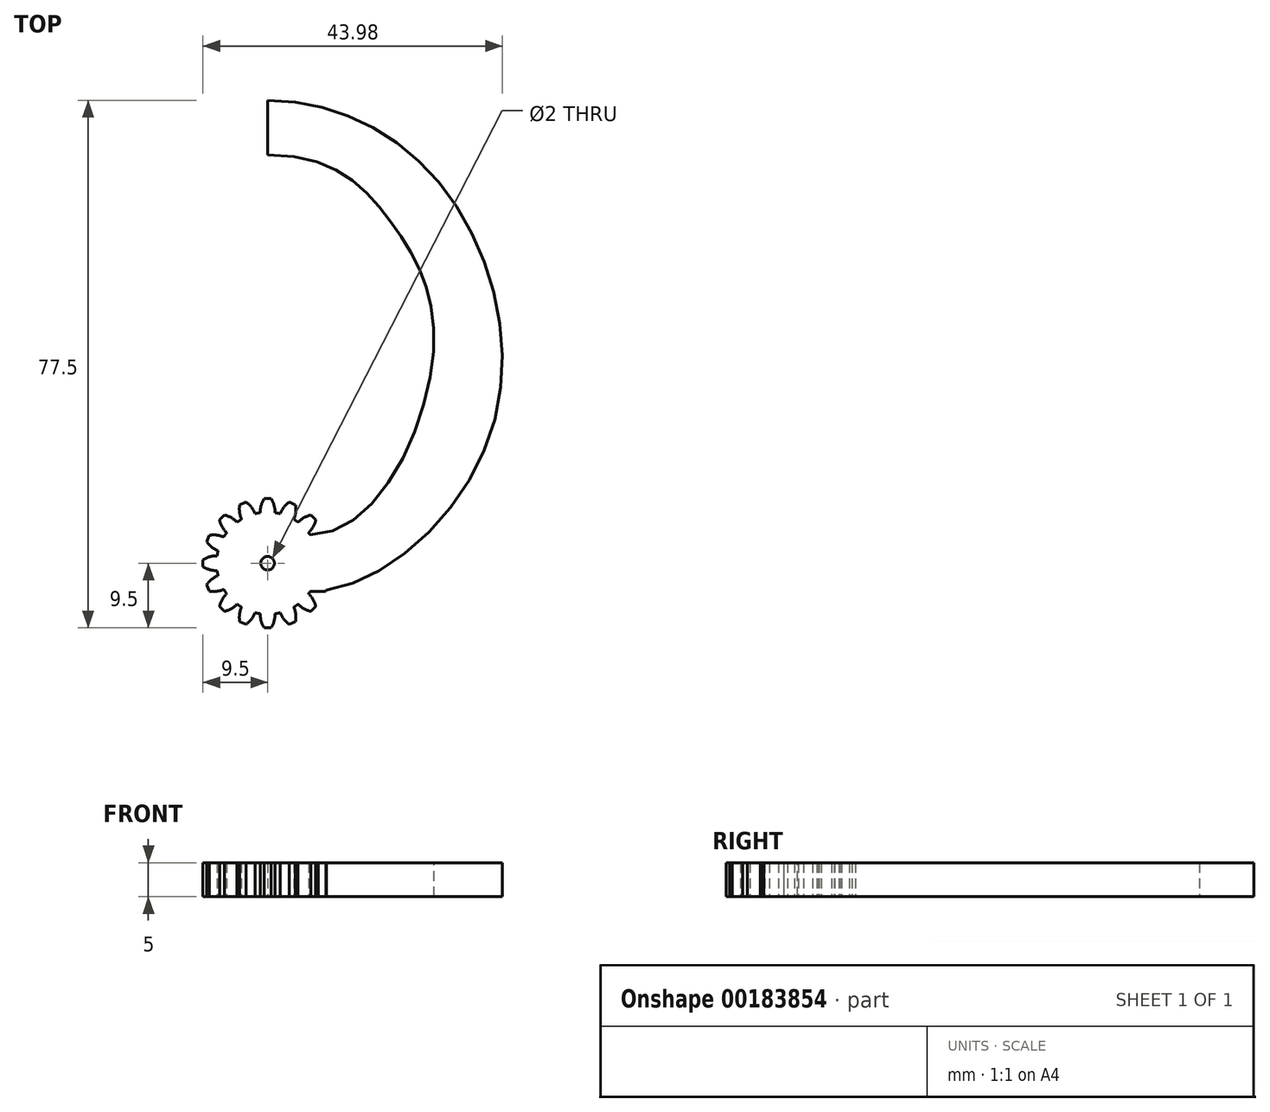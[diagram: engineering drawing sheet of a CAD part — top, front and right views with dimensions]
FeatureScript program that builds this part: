
annotation { "Feature Type Name" : "Feature", "Feature Type Description" : "" }
export const myFeature = defineFeature(function(context is Context, id is Id, definition is map)
    precondition{}
    {
        {
            var Q0;
            Q0=qCreatedBy(makeId("Top.planeOp"),FACE);
            var sketch = newSketch(context, id + "F0", { "sketchPlane" : qUnion([Q0])});
            skCircle(sketch, "E0", {"center": v(0, 0) * mm, "radius": 7.5 * mm});
            skLineSegment(sketch, "E1", {"start": v(0, 0) * mm, "end": v(0, 7.5) * mm, "construction": true});
            skLineSegment(sketch, "E2", {"start": v(0, 9.5) * mm, "end": v(-0.5, 9.5) * mm});
            skArc(sketch, "E3", {"start": v(-0.5, 9.5) * mm, "mid": v(-0.95, 8.5) * mm, "end": v(-1.09, 7.42) * mm});
            skLineSegment(sketch, "E4.MirrorCS", {"start": v(0, 9.5) * mm, "end": v(0.5, 9.5) * mm});
            skArc(sketch, "E5.MirrorCS", {"start": v(0.5, 9.5) * mm, "mid": v(0.95, 8.5) * mm, "end": v(1.09, 7.42) * mm});
            skArc(sketch, "E6.1.0", {"start": v(-4.1, 8.59) * mm, "mid": v(-4.13, 7.5) * mm, "end": v(-3.85, 6.44) * mm});
            skLineSegment(sketch, "E6.1.1", {"start": v(-3.64, 8.78) * mm, "end": v(-4.1, 8.59) * mm});
            skLineSegment(sketch, "E6.1.2", {"start": v(-3.64, 8.78) * mm, "end": v(-3.17, 8.97) * mm});
            skArc(sketch, "E6.1.3", {"start": v(-3.17, 8.97) * mm, "mid": v(-2.38, 8.22) * mm, "end": v(-1.83, 7.27) * mm});
            skArc(sketch, "E6.2.0", {"start": v(-7.07, 6.36) * mm, "mid": v(-6.69, 5.34) * mm, "end": v(-6.02, 4.48) * mm});
            skLineSegment(sketch, "E6.2.1", {"start": v(-6.72, 6.72) * mm, "end": v(-7.07, 6.36) * mm});
            skLineSegment(sketch, "E6.2.2", {"start": v(-6.72, 6.72) * mm, "end": v(-6.36, 7.07) * mm});
            skArc(sketch, "E6.2.3", {"start": v(-6.36, 7.07) * mm, "mid": v(-5.34, 6.69) * mm, "end": v(-4.48, 6.02) * mm});
            skArc(sketch, "E6.3.0", {"start": v(-8.97, 3.17) * mm, "mid": v(-8.22, 2.38) * mm, "end": v(-7.27, 1.83) * mm});
            skLineSegment(sketch, "E6.3.1", {"start": v(-8.78, 3.64) * mm, "end": v(-8.97, 3.17) * mm});
            skLineSegment(sketch, "E6.3.2", {"start": v(-8.78, 3.64) * mm, "end": v(-8.59, 4.1) * mm});
            skArc(sketch, "E6.3.3", {"start": v(-8.59, 4.1) * mm, "mid": v(-7.5, 4.13) * mm, "end": v(-6.44, 3.85) * mm});
            skArc(sketch, "E6.4.0", {"start": v(-9.5, -0.5) * mm, "mid": v(-8.5, -0.95) * mm, "end": v(-7.42, -1.09) * mm});
            skLineSegment(sketch, "E6.4.1", {"start": v(-9.5, 0) * mm, "end": v(-9.5, -0.5) * mm});
            skLineSegment(sketch, "E6.4.2", {"start": v(-9.5, 0) * mm, "end": v(-9.5, 0.5) * mm});
            skArc(sketch, "E6.4.3", {"start": v(-9.5, 0.5) * mm, "mid": v(-8.5, 0.95) * mm, "end": v(-7.42, 1.09) * mm});
            skArc(sketch, "E6.5.0", {"start": v(-8.59, -4.1) * mm, "mid": v(-7.5, -4.13) * mm, "end": v(-6.44, -3.85) * mm});
            skLineSegment(sketch, "E6.5.1", {"start": v(-8.78, -3.64) * mm, "end": v(-8.59, -4.1) * mm});
            skLineSegment(sketch, "E6.5.2", {"start": v(-8.78, -3.64) * mm, "end": v(-8.97, -3.17) * mm});
            skArc(sketch, "E6.5.3", {"start": v(-8.97, -3.17) * mm, "mid": v(-8.22, -2.38) * mm, "end": v(-7.27, -1.83) * mm});
            skArc(sketch, "E6.6.0", {"start": v(-6.36, -7.07) * mm, "mid": v(-5.34, -6.69) * mm, "end": v(-4.48, -6.02) * mm});
            skLineSegment(sketch, "E6.6.1", {"start": v(-6.72, -6.72) * mm, "end": v(-6.36, -7.07) * mm});
            skLineSegment(sketch, "E6.6.2", {"start": v(-6.72, -6.72) * mm, "end": v(-7.07, -6.36) * mm});
            skArc(sketch, "E6.6.3", {"start": v(-7.07, -6.36) * mm, "mid": v(-6.69, -5.34) * mm, "end": v(-6.02, -4.48) * mm});
            skArc(sketch, "E6.7.0", {"start": v(-3.17, -8.97) * mm, "mid": v(-2.38, -8.22) * mm, "end": v(-1.83, -7.27) * mm});
            skLineSegment(sketch, "E6.7.1", {"start": v(-3.64, -8.78) * mm, "end": v(-3.17, -8.97) * mm});
            skLineSegment(sketch, "E6.7.2", {"start": v(-3.64, -8.78) * mm, "end": v(-4.1, -8.59) * mm});
            skArc(sketch, "E6.7.3", {"start": v(-4.1, -8.59) * mm, "mid": v(-4.13, -7.5) * mm, "end": v(-3.85, -6.44) * mm});
            skArc(sketch, "E6.8.0", {"start": v(0.5, -9.5) * mm, "mid": v(0.95, -8.5) * mm, "end": v(1.09, -7.42) * mm});
            skLineSegment(sketch, "E6.8.1", {"start": v(0, -9.5) * mm, "end": v(0.5, -9.5) * mm});
            skLineSegment(sketch, "E6.8.2", {"start": v(0, -9.5) * mm, "end": v(-0.5, -9.5) * mm});
            skArc(sketch, "E6.8.3", {"start": v(-0.5, -9.5) * mm, "mid": v(-0.95, -8.5) * mm, "end": v(-1.09, -7.42) * mm});
            skArc(sketch, "E6.9.0", {"start": v(4.1, -8.59) * mm, "mid": v(4.13, -7.5) * mm, "end": v(3.85, -6.44) * mm});
            skLineSegment(sketch, "E6.9.1", {"start": v(3.64, -8.78) * mm, "end": v(4.1, -8.59) * mm});
            skLineSegment(sketch, "E6.9.2", {"start": v(3.64, -8.78) * mm, "end": v(3.17, -8.97) * mm});
            skArc(sketch, "E6.9.3", {"start": v(3.17, -8.97) * mm, "mid": v(2.38, -8.22) * mm, "end": v(1.83, -7.27) * mm});
            skArc(sketch, "E6.10.0", {"start": v(7.07, -6.36) * mm, "mid": v(6.69, -5.34) * mm, "end": v(6.02, -4.48) * mm});
            skLineSegment(sketch, "E6.10.1", {"start": v(6.72, -6.72) * mm, "end": v(7.07, -6.36) * mm});
            skLineSegment(sketch, "E6.10.2", {"start": v(6.72, -6.72) * mm, "end": v(6.36, -7.07) * mm});
            skArc(sketch, "E6.10.3", {"start": v(6.36, -7.07) * mm, "mid": v(5.34, -6.69) * mm, "end": v(4.48, -6.02) * mm});
            skArc(sketch, "E6.11.0", {"start": v(8.97, -3.17) * mm, "mid": v(8.22, -2.38) * mm, "end": v(7.27, -1.83) * mm});
            skLineSegment(sketch, "E6.11.1", {"start": v(8.78, -3.64) * mm, "end": v(8.97, -3.17) * mm});
            skLineSegment(sketch, "E6.11.2", {"start": v(8.78, -3.64) * mm, "end": v(8.59, -4.1) * mm});
            skArc(sketch, "E6.11.3", {"start": v(8.59, -4.1) * mm, "mid": v(7.5, -4.13) * mm, "end": v(6.44, -3.85) * mm});
            skArc(sketch, "E6.12.0", {"start": v(9.5, 0.5) * mm, "mid": v(8.5, 0.95) * mm, "end": v(7.42, 1.09) * mm});
            skLineSegment(sketch, "E6.12.1", {"start": v(9.5, 0) * mm, "end": v(9.5, 0.5) * mm});
            skLineSegment(sketch, "E6.12.2", {"start": v(9.5, 0) * mm, "end": v(9.5, -0.5) * mm});
            skArc(sketch, "E6.12.3", {"start": v(9.5, -0.5) * mm, "mid": v(8.5, -0.95) * mm, "end": v(7.42, -1.09) * mm});
            skArc(sketch, "E6.13.0", {"start": v(8.59, 4.1) * mm, "mid": v(7.5, 4.13) * mm, "end": v(6.44, 3.85) * mm});
            skLineSegment(sketch, "E6.13.1", {"start": v(8.78, 3.64) * mm, "end": v(8.59, 4.1) * mm});
            skLineSegment(sketch, "E6.13.2", {"start": v(8.78, 3.64) * mm, "end": v(8.97, 3.17) * mm});
            skArc(sketch, "E6.13.3", {"start": v(8.97, 3.17) * mm, "mid": v(8.22, 2.38) * mm, "end": v(7.27, 1.83) * mm});
            skArc(sketch, "E6.14.0", {"start": v(6.36, 7.07) * mm, "mid": v(5.34, 6.69) * mm, "end": v(4.48, 6.02) * mm});
            skLineSegment(sketch, "E6.14.1", {"start": v(6.72, 6.72) * mm, "end": v(6.36, 7.07) * mm});
            skLineSegment(sketch, "E6.14.2", {"start": v(6.72, 6.72) * mm, "end": v(7.07, 6.36) * mm});
            skArc(sketch, "E6.14.3", {"start": v(7.07, 6.36) * mm, "mid": v(6.69, 5.34) * mm, "end": v(6.02, 4.48) * mm});
            skArc(sketch, "E6.15.0", {"start": v(3.17, 8.97) * mm, "mid": v(2.38, 8.22) * mm, "end": v(1.83, 7.27) * mm});
            skLineSegment(sketch, "E6.15.1", {"start": v(3.64, 8.78) * mm, "end": v(3.17, 8.97) * mm});
            skLineSegment(sketch, "E6.15.2", {"start": v(3.64, 8.78) * mm, "end": v(4.1, 8.59) * mm});
            skArc(sketch, "E6.15.3", {"start": v(4.1, 8.59) * mm, "mid": v(4.13, 7.5) * mm, "end": v(3.85, 6.44) * mm});
            skSolve(sketch);
        }
        {
            var Q0;
            Q0=qSketchRegion(id+"F0",true);
            extrude(context, id + "F1", {"entities" : qUnion([Q0]), "depth" : 5 * mm});
        }
        {
            var Q0;
            Q0=makeQuery(id+"F1.opExtrude","CAP_FACE",FACE,{"disambiguationData":[OSD([sQuery(id+"F0.wireOp",EDGE,"E0"),sQuery(id+"F0.wireOp",EDGE,"E2"),sQuery(id+"F0.wireOp",EDGE,"E3"),sQuery(id+"F0.wireOp",EDGE,"E4.MirrorCS"),sQuery(id+"F0.wireOp",EDGE,"E5.MirrorCS"),sQuery(id+"F0.wireOp",EDGE,"E6.1.0"),sQuery(id+"F0.wireOp",EDGE,"E6.1.1"),sQuery(id+"F0.wireOp",EDGE,"E6.1.2"),sQuery(id+"F0.wireOp",EDGE,"E6.1.3"),sQuery(id+"F0.wireOp",EDGE,"E6.2.0"),sQuery(id+"F0.wireOp",EDGE,"E6.2.1"),sQuery(id+"F0.wireOp",EDGE,"E6.2.2"),sQuery(id+"F0.wireOp",EDGE,"E6.2.3"),sQuery(id+"F0.wireOp",EDGE,"E6.3.0"),sQuery(id+"F0.wireOp",EDGE,"E6.3.1"),sQuery(id+"F0.wireOp",EDGE,"E6.3.2"),sQuery(id+"F0.wireOp",EDGE,"E6.3.3"),sQuery(id+"F0.wireOp",EDGE,"E6.4.0"),sQuery(id+"F0.wireOp",EDGE,"E6.4.1"),sQuery(id+"F0.wireOp",EDGE,"E6.4.2"),sQuery(id+"F0.wireOp",EDGE,"E6.4.3"),sQuery(id+"F0.wireOp",EDGE,"E6.5.0"),sQuery(id+"F0.wireOp",EDGE,"E6.5.1"),sQuery(id+"F0.wireOp",EDGE,"E6.5.2"),sQuery(id+"F0.wireOp",EDGE,"E6.5.3"),sQuery(id+"F0.wireOp",EDGE,"E6.6.0"),sQuery(id+"F0.wireOp",EDGE,"E6.6.1"),sQuery(id+"F0.wireOp",EDGE,"E6.6.2"),sQuery(id+"F0.wireOp",EDGE,"E6.6.3"),sQuery(id+"F0.wireOp",EDGE,"E6.7.0"),sQuery(id+"F0.wireOp",EDGE,"E6.7.1"),sQuery(id+"F0.wireOp",EDGE,"E6.7.2"),sQuery(id+"F0.wireOp",EDGE,"E6.7.3"),sQuery(id+"F0.wireOp",EDGE,"E6.8.0"),sQuery(id+"F0.wireOp",EDGE,"E6.8.1"),sQuery(id+"F0.wireOp",EDGE,"E6.8.2"),sQuery(id+"F0.wireOp",EDGE,"E6.8.3"),sQuery(id+"F0.wireOp",EDGE,"E6.9.0"),sQuery(id+"F0.wireOp",EDGE,"E6.9.1"),sQuery(id+"F0.wireOp",EDGE,"E6.9.2"),sQuery(id+"F0.wireOp",EDGE,"E6.9.3"),sQuery(id+"F0.wireOp",EDGE,"E6.10.0"),sQuery(id+"F0.wireOp",EDGE,"E6.10.1"),sQuery(id+"F0.wireOp",EDGE,"E6.10.2"),sQuery(id+"F0.wireOp",EDGE,"E6.10.3"),sQuery(id+"F0.wireOp",EDGE,"E6.11.0"),sQuery(id+"F0.wireOp",EDGE,"E6.11.1"),sQuery(id+"F0.wireOp",EDGE,"E6.11.2"),sQuery(id+"F0.wireOp",EDGE,"E6.11.3"),sQuery(id+"F0.wireOp",EDGE,"E6.12.0"),sQuery(id+"F0.wireOp",EDGE,"E6.12.1"),sQuery(id+"F0.wireOp",EDGE,"E6.12.2"),sQuery(id+"F0.wireOp",EDGE,"E6.12.3"),sQuery(id+"F0.wireOp",EDGE,"E6.13.0"),sQuery(id+"F0.wireOp",EDGE,"E6.13.1"),sQuery(id+"F0.wireOp",EDGE,"E6.13.2"),sQuery(id+"F0.wireOp",EDGE,"E6.13.3"),sQuery(id+"F0.wireOp",EDGE,"E6.14.0"),sQuery(id+"F0.wireOp",EDGE,"E6.14.1"),sQuery(id+"F0.wireOp",EDGE,"E6.14.2"),sQuery(id+"F0.wireOp",EDGE,"E6.14.3"),sQuery(id+"F0.wireOp",EDGE,"E6.15.0"),sQuery(id+"F0.wireOp",EDGE,"E6.15.1"),sQuery(id+"F0.wireOp",EDGE,"E6.15.2"),sQuery(id+"F0.wireOp",EDGE,"E6.15.3")])],"isStart":false});
            var sketch = newSketch(context, id + "F2", { "sketchPlane" : qUnion([Q0])});
            skCircle(sketch, "E7", {"center": v(0, 0) * mm, "radius": 1 * mm});
            skSolve(sketch);
        }
        {
            var Q0;
            Q0=makeQuery(id+"F2.imprint","IMPRINT",FACE,{"disambiguationData":[TD([[makeQuery(id+"F2.imprint","IMPRINT",EDGE,{"derivedFrom":sQuery(id+"F2.wireOp",EDGE,"E7")}),1.0]])]});
            extrude(context, id + "F3", {"entities" : qUnion([Q0]), "operationType" : NewBodyOperationType.REMOVE, "endBound" : BoundingType.THROUGH_ALL, "oppositeDirection" : true, "depth" : 25 * mm});
        }
        {
            var Q0;
            Q0=qCreatedBy(makeId("Top.planeOp"),FACE);
            var sketch = newSketch(context, id + "F4", { "sketchPlane" : qUnion([Q0])});
            skLineSegment(sketch, "E8", {"start": v(0, 68) * mm, "end": v(0, 60) * mm});
            skFitSpline(sketch, "E9", {"points": [v(0, 60) * mm, v(18.26, 49.96) * mm, v(24.32, 30.44) * mm, v(6.24, 4.17) * mm], "startDerivative": vector(96.82, 0) * mm, "endDerivative": vector(-78.26, 0) * mm});
            skFitSpline(sketch, "E10", {"points": [v(0, 68) * mm, v(26.11, 54.74) * mm, v(32.46, 18.18) * mm, v(6.24, -4.17) * mm], "startDerivative": vector(96.3, 0) * mm, "endDerivative": vector(-88.79, 0) * mm});
            skLineSegment(sketch, "E11", {"start": v(6.24, 4.17) * mm, "end": v(6.24, -4.17) * mm});
            skSolve(sketch);
        }
        {
            var Q0;
            Q0=makeQuery(id+"F4.imprint","IMPRINT",FACE,{"disambiguationData":[TD([[makeQuery(id+"F4.imprint","IMPRINT",EDGE,{"derivedFrom":sQuery(id+"F4.wireOp",EDGE,"E8")}),1.0]])]});
            var Q1;
            Q1=makeQuery(id+"F1.opExtrude","CAP_FACE",FACE,{"disambiguationData":[OSD([sQuery(id+"F0.wireOp",EDGE,"E0"),sQuery(id+"F0.wireOp",EDGE,"E2"),sQuery(id+"F0.wireOp",EDGE,"E3"),sQuery(id+"F0.wireOp",EDGE,"E4.MirrorCS"),sQuery(id+"F0.wireOp",EDGE,"E5.MirrorCS"),sQuery(id+"F0.wireOp",EDGE,"E6.1.0"),sQuery(id+"F0.wireOp",EDGE,"E6.1.1"),sQuery(id+"F0.wireOp",EDGE,"E6.1.2"),sQuery(id+"F0.wireOp",EDGE,"E6.1.3"),sQuery(id+"F0.wireOp",EDGE,"E6.2.0"),sQuery(id+"F0.wireOp",EDGE,"E6.2.1"),sQuery(id+"F0.wireOp",EDGE,"E6.2.2"),sQuery(id+"F0.wireOp",EDGE,"E6.2.3"),sQuery(id+"F0.wireOp",EDGE,"E6.3.0"),sQuery(id+"F0.wireOp",EDGE,"E6.3.1"),sQuery(id+"F0.wireOp",EDGE,"E6.3.2"),sQuery(id+"F0.wireOp",EDGE,"E6.3.3"),sQuery(id+"F0.wireOp",EDGE,"E6.4.0"),sQuery(id+"F0.wireOp",EDGE,"E6.4.1"),sQuery(id+"F0.wireOp",EDGE,"E6.4.2"),sQuery(id+"F0.wireOp",EDGE,"E6.4.3"),sQuery(id+"F0.wireOp",EDGE,"E6.5.0"),sQuery(id+"F0.wireOp",EDGE,"E6.5.1"),sQuery(id+"F0.wireOp",EDGE,"E6.5.2"),sQuery(id+"F0.wireOp",EDGE,"E6.5.3"),sQuery(id+"F0.wireOp",EDGE,"E6.6.0"),sQuery(id+"F0.wireOp",EDGE,"E6.6.1"),sQuery(id+"F0.wireOp",EDGE,"E6.6.2"),sQuery(id+"F0.wireOp",EDGE,"E6.6.3"),sQuery(id+"F0.wireOp",EDGE,"E6.7.0"),sQuery(id+"F0.wireOp",EDGE,"E6.7.1"),sQuery(id+"F0.wireOp",EDGE,"E6.7.2"),sQuery(id+"F0.wireOp",EDGE,"E6.7.3"),sQuery(id+"F0.wireOp",EDGE,"E6.8.0"),sQuery(id+"F0.wireOp",EDGE,"E6.8.1"),sQuery(id+"F0.wireOp",EDGE,"E6.8.2"),sQuery(id+"F0.wireOp",EDGE,"E6.8.3"),sQuery(id+"F0.wireOp",EDGE,"E6.9.0"),sQuery(id+"F0.wireOp",EDGE,"E6.9.1"),sQuery(id+"F0.wireOp",EDGE,"E6.9.2"),sQuery(id+"F0.wireOp",EDGE,"E6.9.3"),sQuery(id+"F0.wireOp",EDGE,"E6.10.0"),sQuery(id+"F0.wireOp",EDGE,"E6.10.1"),sQuery(id+"F0.wireOp",EDGE,"E6.10.2"),sQuery(id+"F0.wireOp",EDGE,"E6.10.3"),sQuery(id+"F0.wireOp",EDGE,"E6.11.0"),sQuery(id+"F0.wireOp",EDGE,"E6.11.1"),sQuery(id+"F0.wireOp",EDGE,"E6.11.2"),sQuery(id+"F0.wireOp",EDGE,"E6.11.3"),sQuery(id+"F0.wireOp",EDGE,"E6.12.0"),sQuery(id+"F0.wireOp",EDGE,"E6.12.1"),sQuery(id+"F0.wireOp",EDGE,"E6.12.2"),sQuery(id+"F0.wireOp",EDGE,"E6.12.3"),sQuery(id+"F0.wireOp",EDGE,"E6.13.0"),sQuery(id+"F0.wireOp",EDGE,"E6.13.1"),sQuery(id+"F0.wireOp",EDGE,"E6.13.2"),sQuery(id+"F0.wireOp",EDGE,"E6.13.3"),sQuery(id+"F0.wireOp",EDGE,"E6.14.0"),sQuery(id+"F0.wireOp",EDGE,"E6.14.1"),sQuery(id+"F0.wireOp",EDGE,"E6.14.2"),sQuery(id+"F0.wireOp",EDGE,"E6.14.3"),sQuery(id+"F0.wireOp",EDGE,"E6.15.0"),sQuery(id+"F0.wireOp",EDGE,"E6.15.1"),sQuery(id+"F0.wireOp",EDGE,"E6.15.2"),sQuery(id+"F0.wireOp",EDGE,"E6.15.3")])],"isStart":false});
            extrude(context, id + "F5", {"entities" : qUnion([Q0]), "operationType" : NewBodyOperationType.ADD, "endBound" : BoundingType.UP_TO_SURFACE, "endBoundEntityFace" : qUnion([Q1]), "depth" : 25 * mm});
        }
    });
